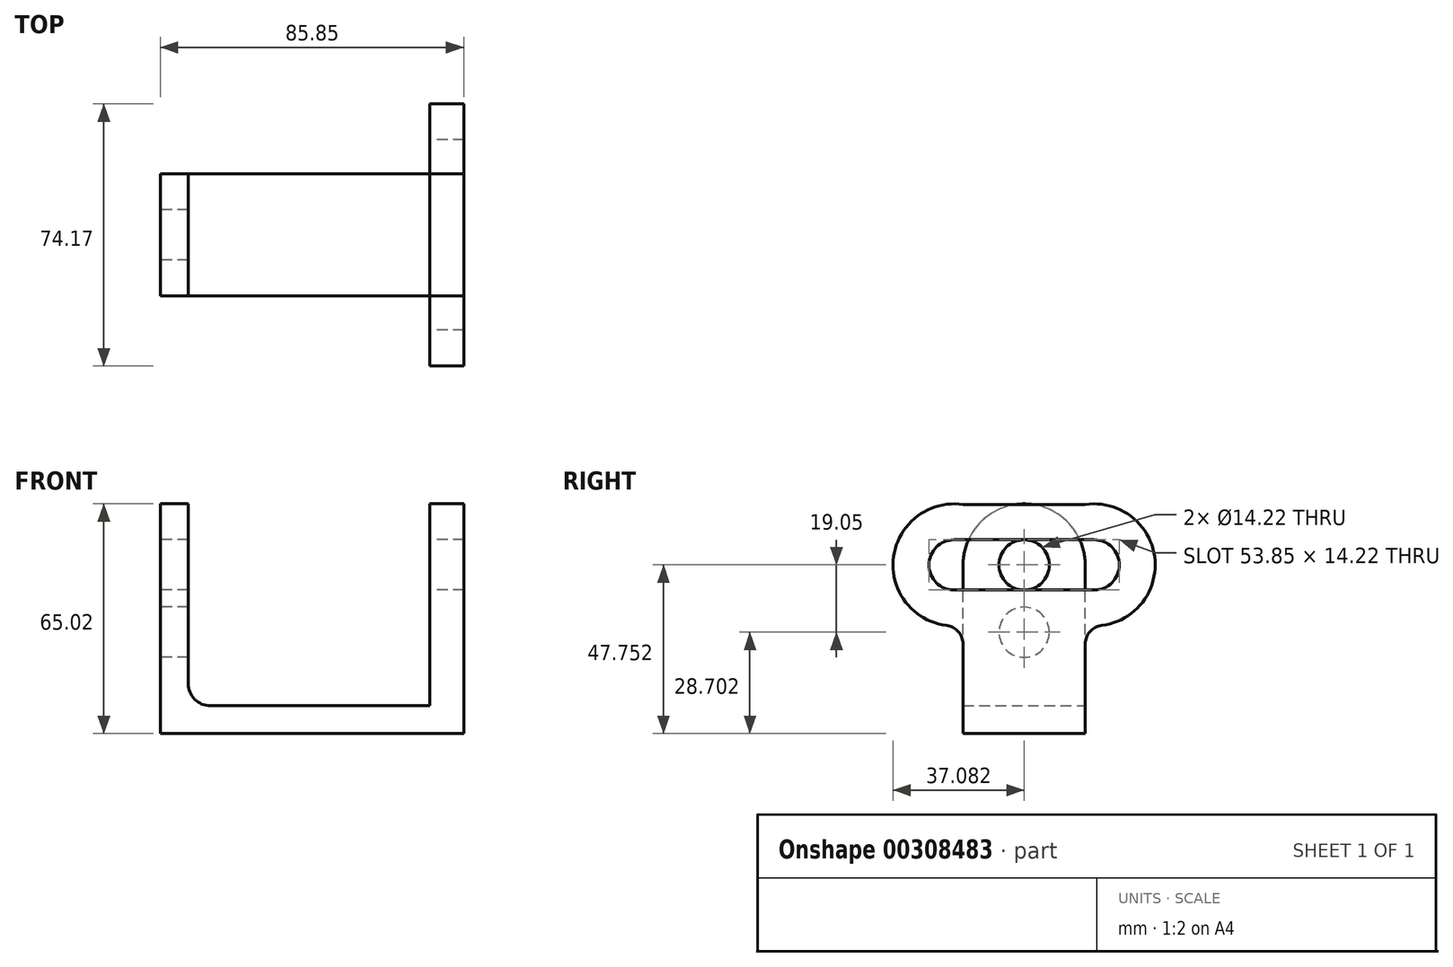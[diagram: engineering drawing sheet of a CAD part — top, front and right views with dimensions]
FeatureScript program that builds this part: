
annotation { "Feature Type Name" : "Feature", "Feature Type Description" : "" }
export const myFeature = defineFeature(function(context is Context, id is Id, definition is map)
    precondition{}
    {
        {
            var Q0;
            Q0=qCreatedBy(makeId("Right.planeOp"),FACE);
            var sketch = newSketch(context, id + "F0", { "sketchPlane" : qUnion([Q0])});
            skLineSegment(sketch, "E0", {"start": v(0, 0) * mm, "end": v(34.54, 0) * mm});
            skLineSegment(sketch, "E1", {"start": v(0, 0) * mm, "end": v(0, 25.32) * mm});
            skArc(sketch, "E2", {"start": v(0, 64.84) * mm, "mid": v(-19.65, 50.09) * mm, "end": v(-4.67, 30.61) * mm});
            skLineSegment(sketch, "E3", {"start": v(34.54, 0) * mm, "end": v(34.54, 25.32) * mm});
            skArc(sketch, "E4", {"start": v(39.22, 30.61) * mm, "mid": v(54.2, 50.09) * mm, "end": v(34.54, 64.84) * mm});
            skLineSegment(sketch, "E5", {"start": v(0, 64.84) * mm, "end": v(34.54, 64.84) * mm});
            skArc(sketch, "E6", {"start": v(37.08, 40.64) * mm, "mid": v(44.2, 47.75) * mm, "end": v(37.08, 54.86) * mm});
            skArc(sketch, "E7", {"start": v(-2.54, 54.86) * mm, "mid": v(-9.65, 47.75) * mm, "end": v(-2.54, 40.64) * mm});
            skPoint(sketch, "E8.visualSharp", {"position": v(0, 30.67) * mm});
            skArc(sketch, "E8.filletArc", {"start": v(0, 25.32) * mm, "mid": v(-1.34, 28.85) * mm, "end": v(-4.67, 30.61) * mm});
            skPoint(sketch, "E9.visualSharp", {"position": v(34.54, 30.67) * mm});
            skArc(sketch, "E9.filletArc", {"start": v(39.22, 30.61) * mm, "mid": v(35.88, 28.85) * mm, "end": v(34.54, 25.32) * mm});
            skLineSegment(sketch, "E10", {"start": v(-2.54, 54.86) * mm, "end": v(37.08, 54.86) * mm});
            skLineSegment(sketch, "E11", {"start": v(-2.54, 40.64) * mm, "end": v(37.08, 40.64) * mm});
            skSolve(sketch);
        }
        {
            var Q0;
            Q0 = qSketchRegion(id + "F0", true);
            extrude(context, id + "F1", {"entities" : qUnion([Q0]), "depth" : 9.65 * mm});
        }
        {
            var Q0;
            Q0=qCreatedBy(makeId("Front.planeOp"),FACE);
            var sketch = newSketch(context, id + "F2", { "sketchPlane" : qUnion([Q0])});
            skLineSegment(sketch, "E12", {"start": v(0, 0) * mm, "end": v(-76.2, 0) * mm});
            skLineSegment(sketch, "E13", {"start": v(-76.2, 0) * mm, "end": v(-76.2, 7.87) * mm});
            skLineSegment(sketch, "E14", {"start": v(-76.2, 7.87) * mm, "end": v(0, 7.87) * mm});
            skLineSegment(sketch, "E15", {"start": v(0, 7.87) * mm, "end": v(0, 0) * mm});
            skSolve(sketch);
        }
        {
            var Q0;
            Q0 = qSketchRegion(id + "F2", true);
            extrude(context, id + "F3", {"entities" : qUnion([Q0]), "operationType" : NewBodyOperationType.ADD, "oppositeDirection" : true, "depth" : 34.54 * mm});
        }
        {
            var Q0;
            Q0=makeQuery(id+"F3.opExtrude","SWEPT_FACE",FACE,{"disambiguationData":[OSD([sQuery(id+"F2.wireOp",EDGE,"E13")])]});
            var sketch = newSketch(context, id + "F4", { "sketchPlane" : qUnion([Q0])});
            skLineSegment(sketch, "E16", {"start": v(-34.54, 0) * mm, "end": v(-34.54, 47.75) * mm});
            skPoint(sketch, "E16.endSnap0", {"position": v(-34.54, 3.94) * mm});
            skLineSegment(sketch, "E17", {"start": v(-34.54, 0) * mm, "end": v(0, 0) * mm});
            skLineSegment(sketch, "E18", {"start": v(0, 0) * mm, "end": v(0, 47.75) * mm});
            skPoint(sketch, "E18.endSnap0", {"position": v(0, 3.94) * mm});
            skArc(sketch, "E19", {"start": v(0, 47.75) * mm, "mid": v(-17.27, 65.02) * mm, "end": v(-34.54, 47.75) * mm});
            skCircle(sketch, "E20", {"center": v(-17.27, 47.75) * mm, "radius": 7.11 * mm});
            skCircle(sketch, "E21", {"center": v(-17.27, 28.7) * mm, "radius": 7.11 * mm});
            skSolve(sketch);
        }
        {
            var Q0;
            Q0 = qSketchRegion(id + "F4", true);
            extrude(context, id + "F5", {"entities" : qUnion([Q0]), "operationType" : NewBodyOperationType.ADD, "oppositeDirection" : true, "depth" : 7.87 * mm});
        }
        {
            var Q0;
            Q0=makeQuery(id+"F5.boolean.opBoolean","INTERSECT",EDGE,{"derivedFrom":[makeQuery(id+"F3.opExtrude","SWEPT_FACE",FACE,{"disambiguationData":[OSD([sQuery(id+"F2.wireOp",EDGE,"E14")])]}),makeQuery(id+"F5.opExtrude","CAP_FACE",FACE,{"disambiguationData":[OSD([sQuery(id+"F4.wireOp",EDGE,"E16"),sQuery(id+"F4.wireOp",EDGE,"E17"),sQuery(id+"F4.wireOp",EDGE,"E18"),sQuery(id+"F4.wireOp",EDGE,"E19"),sQuery(id+"F4.wireOp",EDGE,"E20"),sQuery(id+"F4.wireOp",EDGE,"E21")])],"isStart":false})]});
            var Q1;
            Q1=makeQuery(id+"F3.opExtrude","SWEPT_EDGE",EDGE,{"disambiguationData":[OSD([sQuery(id+"F2.wireOp",EDGE,"E14"),sQuery(id+"F2.wireOp",EDGE,"E15")])]});
            fillet(context, id + "F6", {"entities" : qUnion([Q0, Q1]), "radius" : 6.35 * mm, "tangentPropagation" : true, "allowEdgeOverflow" : false});
        }
    });
